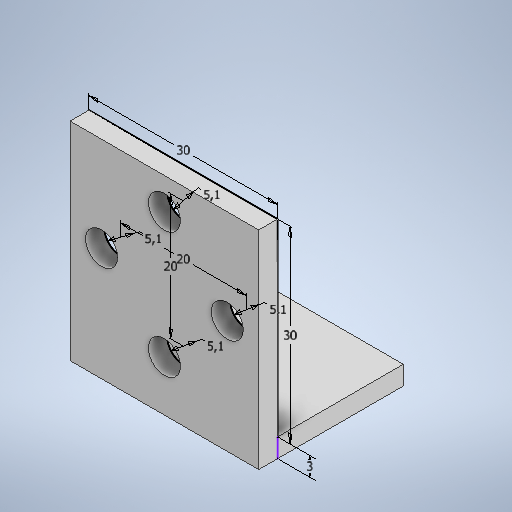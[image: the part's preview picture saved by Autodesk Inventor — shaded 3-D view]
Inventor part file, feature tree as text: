
AUTODESK INVENTOR PART (.ipt)
format: ipt  version: 2025.2 (Build 292293000, 293)  size: 242,688 bytes
history: native  units: mm
features: extrude x2, sketch x1
ambient origin geometry x8: Origin, YZ Plane, XZ Plane, XY Plane, X Axis, Y Axis, Z Axis, Center Point
bodies: Solid1 (feature_tree)
feature tree (3):
  sketch  "Sketch1"  dims[d0=30.0mm d1=30.0mm d2=20.0mm d3=20.0mm d4=5.1mm d5=5.1mm d6=5.1mm d7=5.1mm d8=3.0mm d9=3.0mm d10=0.0mm d11=20.0mm d12=0.0mm]
  extrude  "Extrusion1"  Depth=30.0mm
  extrude  "Extrusion2"  Depth=20.0mm
